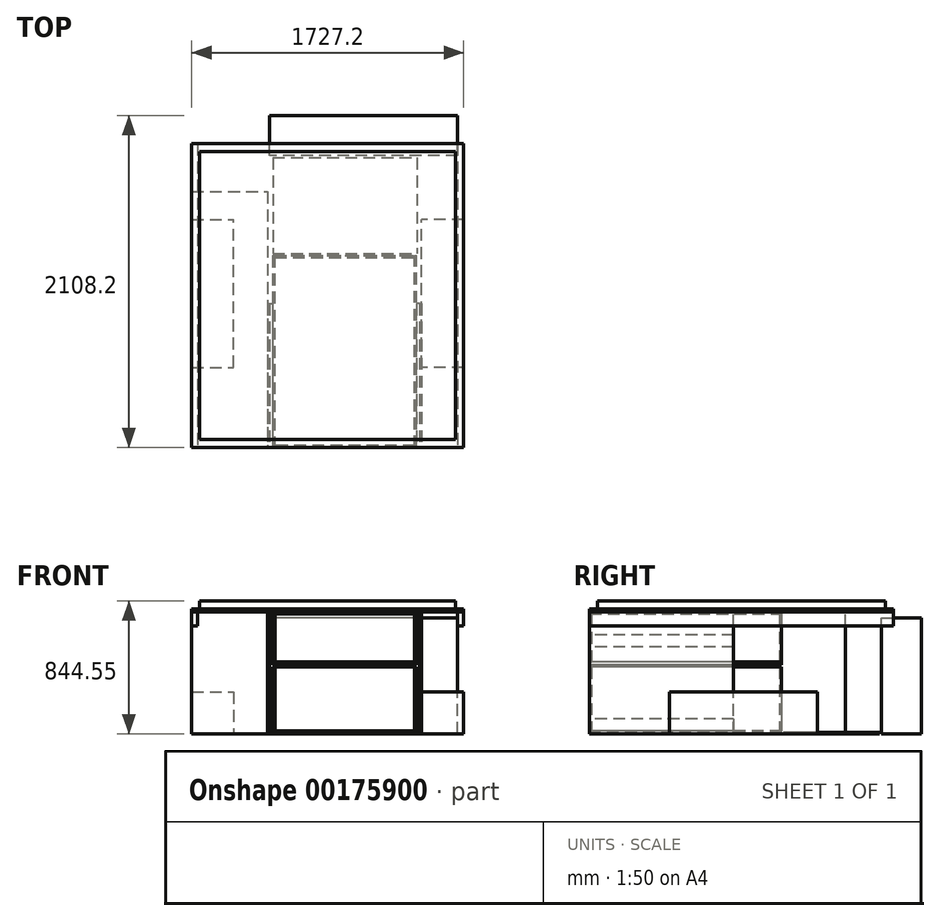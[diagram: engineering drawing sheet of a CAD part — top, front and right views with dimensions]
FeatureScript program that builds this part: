
annotation { "Feature Type Name" : "Feature", "Feature Type Description" : "" }
export const myFeature = defineFeature(function(context is Context, id is Id, definition is map)
    precondition{}
    {
        {
            var Q0;
            Q0=qCreatedBy(makeId("Front.planeOp"),FACE);
            var sketch = newSketch(context, id + "F0", { "sketchPlane" : qUnion([Q0])});
            skLineSegment(sketch, "E0.bottom", {"start": v(-863.6, 793.75) * mm, "end": v(863.6, 793.75) * mm});
            skLineSegment(sketch, "E0.top", {"start": v(-863.6, 774.7) * mm, "end": v(863.6, 774.7) * mm});
            skLineSegment(sketch, "E0.left", {"start": v(-863.6, 793.75) * mm, "end": v(-863.6, 774.7) * mm});
            skLineSegment(sketch, "E0.right", {"start": v(863.6, 793.75) * mm, "end": v(863.6, 774.7) * mm});
            skLineSegment(sketch, "E1", {"start": v(0, 774.7) * mm, "end": v(0, 0) * mm, "construction": true});
            skLineSegment(sketch, "E2.bottom", {"start": v(825.5, 774.45) * mm, "end": v(863.6, 774.45) * mm});
            skLineSegment(sketch, "E2.top", {"start": v(825.5, 685.55) * mm, "end": v(863.6, 685.55) * mm});
            skLineSegment(sketch, "E2.left", {"start": v(825.5, 774.45) * mm, "end": v(825.5, 685.55) * mm});
            skLineSegment(sketch, "E2.right", {"start": v(863.6, 774.45) * mm, "end": v(863.6, 685.55) * mm});
            skLineSegment(sketch, "E3.MirrorCS", {"start": v(-863.6, 774.45) * mm, "end": v(-863.6, 685.55) * mm});
            skLineSegment(sketch, "E4.MirrorCS", {"start": v(-825.5, 774.45) * mm, "end": v(-825.5, 685.55) * mm});
            skLineSegment(sketch, "E5.MirrorCS", {"start": v(-825.5, 774.45) * mm, "end": v(-863.6, 774.45) * mm});
            skLineSegment(sketch, "E6.MirrorCS", {"start": v(-825.5, 685.55) * mm, "end": v(-863.6, 685.55) * mm});
            skSolve(sketch);
        }
        {
            var Q0;
            Q0 = qSketchRegion(id + "F0", true);
            extrude(context, id + "F1", {"entities" : qUnion([Q0]), "oppositeDirection" : true, "depth" : 1930.4 * mm});
        }
        {
            var Q0;
            Q0=qCreatedBy(makeId("Top.planeOp"),FACE);
            var sketch = newSketch(context, id + "F2", { "sketchPlane" : qUnion([Q0])});
            skLineSegment(sketch, "E7.0.0", {"start": v(-863.6, 0) * mm, "end": v(863.6, 0) * mm});
            skLineSegment(sketch, "E7.0.1", {"start": v(863.6, 0) * mm, "end": v(863.6, 1930.4) * mm});
            skLineSegment(sketch, "E7.0.2", {"start": v(863.6, 1930.4) * mm, "end": v(-863.6, 1930.4) * mm});
            skLineSegment(sketch, "E7.0.3", {"start": v(-863.6, 1930.4) * mm, "end": v(-863.6, 0) * mm});
            skSolve(sketch);
        }
        {
            var Q0;
            Q0=qCreatedBy(makeId("Top.planeOp"),FACE);
            var sketch = newSketch(context, id + "F3", { "sketchPlane" : qUnion([Q0])});
            skLineSegment(sketch, "E8.bottom", {"start": v(863.6, 508) * mm, "end": v(596.9, 508) * mm});
            skLineSegment(sketch, "E8.top", {"start": v(863.6, 1447.8) * mm, "end": v(596.9, 1447.8) * mm});
            skLineSegment(sketch, "E8.left", {"start": v(863.6, 508) * mm, "end": v(863.6, 1447.8) * mm});
            skLineSegment(sketch, "E8.right", {"start": v(596.9, 508) * mm, "end": v(596.9, 1447.8) * mm});
            skLineSegment(sketch, "E9", {"start": v(0, 0) * mm, "end": v(0, 438.64) * mm, "construction": true});
            skLineSegment(sketch, "E10.MirrorCS", {"start": v(-863.6, 1447.8) * mm, "end": v(-596.9, 1447.8) * mm});
            skLineSegment(sketch, "E11.MirrorCS", {"start": v(-863.6, 508) * mm, "end": v(-596.9, 508) * mm});
            skLineSegment(sketch, "E12.MirrorCS", {"start": v(-863.6, 508) * mm, "end": v(-863.6, 1447.8) * mm});
            skLineSegment(sketch, "E13.MirrorCS", {"start": v(-596.9, 508) * mm, "end": v(-596.9, 1447.8) * mm});
            skSolve(sketch);
        }
        {
            var Q0;
            Q0 = qSketchRegion(id + "F3", true);
            extrude(context, id + "F4", {"entities" : qUnion([Q0]), "depth" : 266.7 * mm});
        }
        {
            var Q0;
            Q0=qCreatedBy(makeId("Front.planeOp"),FACE);
            var sketch = newSketch(context, id + "F5", { "sketchPlane" : qUnion([Q0])});
            skLineSegment(sketch, "E14.bottom", {"start": v(-381, 774.7) * mm, "end": v(-368.3, 774.7) * mm});
            skLineSegment(sketch, "E14.top", {"start": v(-381, 0) * mm, "end": v(-368.3, 0) * mm});
            skLineSegment(sketch, "E14.left", {"start": v(-381, 774.7) * mm, "end": v(-381, 0) * mm});
            skLineSegment(sketch, "E14.right", {"start": v(-368.3, 774.7) * mm, "end": v(-368.3, 0) * mm});
            skLineSegment(sketch, "E15.bottom", {"start": v(584.2, 0) * mm, "end": v(596.9, 0) * mm});
            skLineSegment(sketch, "E15.top", {"start": v(584.2, 774.7) * mm, "end": v(596.9, 774.7) * mm});
            skLineSegment(sketch, "E15.left", {"start": v(584.2, 0) * mm, "end": v(584.2, 774.7) * mm});
            skLineSegment(sketch, "E15.right", {"start": v(596.9, 0) * mm, "end": v(596.9, 774.7) * mm});
            skSolve(sketch);
        }
        {
            var Q0;
            Q0 = qSketchRegion(id + "F5", true);
            extrude(context, id + "F6", {"entities" : qUnion([Q0]), "oppositeDirection" : true, "depth" : 914.4 * mm});
        }
        {
            var Q0;
            Q0=qCreatedBy(makeId("Front.planeOp"),FACE);
            var sketch = newSketch(context, id + "F7", { "sketchPlane" : qUnion([Q0])});
            skLineSegment(sketch, "E16.bottom", {"start": v(-349.25, 95.25) * mm, "end": v(-368.3, 95.25) * mm});
            skLineSegment(sketch, "E16.top", {"start": v(-349.25, 19.05) * mm, "end": v(-368.3, 19.05) * mm});
            skLineSegment(sketch, "E16.left", {"start": v(-349.25, 95.25) * mm, "end": v(-349.25, 19.05) * mm});
            skLineSegment(sketch, "E16.right", {"start": v(-368.3, 95.25) * mm, "end": v(-368.3, 19.05) * mm});
            skLineSegment(sketch, "E17.bottom", {"start": v(565.15, 19.05) * mm, "end": v(584.2, 19.05) * mm});
            skLineSegment(sketch, "E17.top", {"start": v(565.15, 95.25) * mm, "end": v(584.2, 95.25) * mm});
            skLineSegment(sketch, "E17.left", {"start": v(565.15, 19.05) * mm, "end": v(565.15, 95.25) * mm});
            skLineSegment(sketch, "E17.right", {"start": v(584.2, 19.05) * mm, "end": v(584.2, 95.25) * mm});
            skLineSegment(sketch, "E18.bottom", {"start": v(-368.3, 628.65) * mm, "end": v(-349.25, 628.65) * mm});
            skLineSegment(sketch, "E18.top", {"start": v(-368.3, 552.45) * mm, "end": v(-349.25, 552.45) * mm});
            skLineSegment(sketch, "E18.left", {"start": v(-368.3, 628.65) * mm, "end": v(-368.3, 552.45) * mm});
            skLineSegment(sketch, "E18.right", {"start": v(-349.25, 628.65) * mm, "end": v(-349.25, 552.45) * mm});
            skPoint(sketch, "E18.middle", {"position": v(-358.78, 590.55) * mm});
            skLineSegment(sketch, "E19.bottom", {"start": v(584.2, 628.65) * mm, "end": v(565.15, 628.65) * mm});
            skLineSegment(sketch, "E19.top", {"start": v(584.2, 552.45) * mm, "end": v(565.15, 552.45) * mm});
            skLineSegment(sketch, "E19.left", {"start": v(584.2, 628.65) * mm, "end": v(584.2, 552.45) * mm});
            skLineSegment(sketch, "E19.right", {"start": v(565.15, 628.65) * mm, "end": v(565.15, 552.45) * mm});
            skPoint(sketch, "E19.middle", {"position": v(574.67, 590.55) * mm});
            skSolve(sketch);
        }
        {
            var Q0;
            Q0 = qSketchRegion(id + "F7", true);
            extrude(context, id + "F8", {"entities" : qUnion([Q0]), "oppositeDirection" : true, "depth" : 914.4 * mm});
        }
        {
            var Q0;
            Q0=qCreatedBy(makeId("Front.planeOp"),FACE);
            var sketch = newSketch(context, id + "F9", { "sketchPlane" : qUnion([Q0])});
            skLineSegment(sketch, "E20.bottom", {"start": v(-349.25, 9.52) * mm, "end": v(565.15, 9.53) * mm});
            skLineSegment(sketch, "E20.top", {"start": v(-349.25, 19.05) * mm, "end": v(565.15, 19.05) * mm});
            skLineSegment(sketch, "E20.left", {"start": v(-349.25, 9.53) * mm, "end": v(-349.25, 19.05) * mm});
            skLineSegment(sketch, "E20.right", {"start": v(565.15, 9.53) * mm, "end": v(565.15, 19.05) * mm});
            skSolve(sketch);
        }
        {
            var Q0;
            Q0=makeQuery(id+"F9.imprint","IMPRINT",FACE,{"disambiguationData":[TD([[makeQuery(id+"F9.imprint","IMPRINT",EDGE,{"derivedFrom":sQuery(id+"F9.wireOp",EDGE,"E20.bottom")}),1.0]])]});
            extrude(context, id + "F10", {"entities" : qUnion([Q0]), "oppositeDirection" : true, "depth" : 1219.2 * mm});
        }
        {
            var Q0;
            Q0=makeQuery(id+"F10.opExtrude","SWEPT_FACE",FACE,{"disambiguationData":[OSD([sQuery(id+"F9.wireOp",EDGE,"E20.top")])]});
            var sketch = newSketch(context, id + "F11", { "sketchPlane" : qUnion([Q0])});
            skLineSegment(sketch, "E21.bottom", {"start": v(-349.25, 1219.2) * mm, "end": v(-336.55, 1219.2) * mm});
            skLineSegment(sketch, "E21.top", {"start": v(-349.25, 0) * mm, "end": v(-336.55, 0) * mm});
            skLineSegment(sketch, "E21.left", {"start": v(-349.25, 1219.2) * mm, "end": v(-349.25, 0) * mm});
            skLineSegment(sketch, "E21.right", {"start": v(-336.55, 1219.2) * mm, "end": v(-336.55, 0) * mm});
            skLineSegment(sketch, "E22.bottom", {"start": v(565.15, 0) * mm, "end": v(552.45, 0) * mm});
            skLineSegment(sketch, "E22.top", {"start": v(565.15, 1219.2) * mm, "end": v(552.45, 1219.2) * mm});
            skLineSegment(sketch, "E22.left", {"start": v(565.15, 0) * mm, "end": v(565.15, 1219.2) * mm});
            skLineSegment(sketch, "E22.right", {"start": v(552.45, 0) * mm, "end": v(552.45, 1219.2) * mm});
            skLineSegment(sketch, "E23.bottom", {"start": v(-336.3, 1219.2) * mm, "end": v(552.2, 1219.2) * mm});
            skLineSegment(sketch, "E23.top", {"start": v(-336.3, 1206.5) * mm, "end": v(552.2, 1206.5) * mm});
            skLineSegment(sketch, "E23.left", {"start": v(552.2, 1219.2) * mm, "end": v(552.2, 1206.5) * mm});
            skLineSegment(sketch, "E23.right", {"start": v(-336.3, 1219.2) * mm, "end": v(-336.3, 1206.5) * mm});
            skLineSegment(sketch, "E24.bottom", {"start": v(552.2, 0) * mm, "end": v(-336.3, 0) * mm});
            skLineSegment(sketch, "E24.top", {"start": v(552.2, 12.7) * mm, "end": v(-336.3, 12.7) * mm});
            skLineSegment(sketch, "E24.left", {"start": v(552.2, 0) * mm, "end": v(552.2, 12.7) * mm});
            skLineSegment(sketch, "E24.right", {"start": v(-336.3, 0) * mm, "end": v(-336.3, 12.7) * mm});
            skSolve(sketch);
        }
        {
            var Q0;
            Q0 = qSketchRegion(id + "F11", true);
            extrude(context, id + "F12", {"entities" : qUnion([Q0]), "depth" : 406.4 * mm, "offsetDistance" : 25.4 * mm});
        }
        {
            var Q0;
            Q0=makeQuery(id+"F1.opExtrude","SWEPT_FACE",FACE,{"disambiguationData":[OSD([sQuery(id+"F0.wireOp",EDGE,"E0.bottom")])]});
            var sketch = newSketch(context, id + "F13", { "sketchPlane" : qUnion([Q0])});
            skLineSegment(sketch, "E25.0", {"start": v(-812.8, 50.8) * mm, "end": v(812.8, 50.8) * mm});
            skLineSegment(sketch, "E25.1", {"start": v(-812.8, 1879.6) * mm, "end": v(-812.8, 50.8) * mm});
            skLineSegment(sketch, "E25.2", {"start": v(812.8, 1879.6) * mm, "end": v(-812.8, 1879.6) * mm});
            skLineSegment(sketch, "E25.3", {"start": v(812.8, 50.8) * mm, "end": v(812.8, 1879.6) * mm});
            skSolve(sketch);
        }
        {
            var Q0;
            Q0 = qSketchRegion(id + "F13", true);
            extrude(context, id + "F14", {"entities" : qUnion([Q0]), "operationType" : NewBodyOperationType.ADD, "depth" : 50.8 * mm});
        }
        {
            var Q0;
            Q0=makeQuery(id+"F1.opExtrude","CAP_FACE",FACE,{"disambiguationData":[OSD([sQuery(id+"F0.wireOp",EDGE,"E0.bottom"),sQuery(id+"F0.wireOp",EDGE,"E0.top"),sQuery(id+"F0.wireOp",EDGE,"E0.left"),sQuery(id+"F0.wireOp",EDGE,"E0.right")])],"isStart":false});
            var sketch = newSketch(context, id + "F15", { "sketchPlane" : qUnion([Q0])});
            skLineSegment(sketch, "E26.bottom", {"start": v(-825.5, 0) * mm, "end": v(368.3, 0) * mm});
            skLineSegment(sketch, "E26.top", {"start": v(-825.5, 736.6) * mm, "end": v(368.3, 736.6) * mm});
            skLineSegment(sketch, "E26.left", {"start": v(-825.5, 0) * mm, "end": v(-825.5, 736.6) * mm});
            skLineSegment(sketch, "E26.right", {"start": v(368.3, 0) * mm, "end": v(368.3, 736.6) * mm});
            skSolve(sketch);
        }
        {
            var Q0;
            Q0 = qSketchRegion(id + "F15", true);
            extrude(context, id + "F16", {"entities" : qUnion([Q0]), "oppositeDirection" : true, "depth" : 76.2 * mm, "hasSecondDirection" : true, "secondDirectionOppositeDirection" : false, "secondDirectionDepth" : 177.8 * mm});
        }
        {
            var Q0;
            Q0=makeQuery(id+"F1.opExtrude","CAP_FACE",FACE,{"disambiguationData":[OSD([sQuery(id+"F0.wireOp",EDGE,"E3.MirrorCS"),sQuery(id+"F0.wireOp",EDGE,"E4.MirrorCS"),sQuery(id+"F0.wireOp",EDGE,"E5.MirrorCS"),sQuery(id+"F0.wireOp",EDGE,"E6.MirrorCS")])],"isStart":true});
            var sketch = newSketch(context, id + "F17", { "sketchPlane" : qUnion([Q0])});
            skLineSegment(sketch, "E27.bottom", {"start": v(-863.6, 0) * mm, "end": v(-381, 0) * mm});
            skLineSegment(sketch, "E27.top", {"start": v(-863.6, 774.7) * mm, "end": v(-381, 774.7) * mm});
            skLineSegment(sketch, "E27.left", {"start": v(-863.6, 0) * mm, "end": v(-863.6, 774.7) * mm});
            skLineSegment(sketch, "E27.right", {"start": v(-381, 0) * mm, "end": v(-381, 774.7) * mm});
            skSolve(sketch);
        }
        {
            var Q0;
            Q0 = qSketchRegion(id + "F17", true);
            extrude(context, id + "F18", {"entities" : qUnion([Q0]), "oppositeDirection" : true, "depth" : 1625.6 * mm});
        }
        {
            var Q0;
            Q0=qCreatedBy(makeId("Top.planeOp"),FACE);
            var sketch = newSketch(context, id + "F19", { "sketchPlane" : qUnion([Q0])});
            skLineSegment(sketch, "E28.bottom", {"start": v(-348.45, 1841.16) * mm, "end": v(565.95, 1841.16) * mm});
            skLineSegment(sketch, "E28.top", {"start": v(-348.45, 1231.56) * mm, "end": v(565.95, 1231.56) * mm});
            skLineSegment(sketch, "E28.left", {"start": v(-348.45, 1841.16) * mm, "end": v(-348.45, 1231.56) * mm});
            skLineSegment(sketch, "E28.right", {"start": v(565.95, 1841.16) * mm, "end": v(565.95, 1231.56) * mm});
            skSolve(sketch);
        }
        {
            var Q0;
            Q0 = qSketchRegion(id + "F19", true);
            extrude(context, id + "F20", {"entities" : qUnion([Q0]), "depth" : 9.52 * mm});
        }
        {
            var Q0;
            Q0=makeQuery(id+"F10.opExtrude","CAP_FACE",FACE,{"disambiguationData":[OSD([sQuery(id+"F9.wireOp",EDGE,"E20.bottom"),sQuery(id+"F9.wireOp",EDGE,"E20.top"),sQuery(id+"F9.wireOp",EDGE,"E20.left"),sQuery(id+"F9.wireOp",EDGE,"E20.right")])],"isStart":true});
            var sketch = newSketch(context, id + "F21", { "sketchPlane" : qUnion([Q0])});
            skLineSegment(sketch, "E29.bottom", {"start": v(-349.25, 438.15) * mm, "end": v(565.15, 438.15) * mm});
            skLineSegment(sketch, "E29.top", {"start": v(-349.25, 457.2) * mm, "end": v(565.15, 457.2) * mm});
            skLineSegment(sketch, "E29.left", {"start": v(-349.25, 438.15) * mm, "end": v(-349.25, 457.2) * mm});
            skLineSegment(sketch, "E29.right", {"start": v(565.15, 438.15) * mm, "end": v(565.15, 457.2) * mm});
            skSolve(sketch);
        }
        {
            var Q0;
            Q0=makeQuery(id+"F21.imprint","IMPRINT",FACE,{"disambiguationData":[TD([[makeQuery(id+"F21.imprint","IMPRINT",EDGE,{"derivedFrom":sQuery(id+"F21.wireOp",EDGE,"E29.bottom")}),1.0]])]});
            var Q1;
            Q1=makeQuery(id+"F10.opExtrude","CAP_FACE",FACE,{"disambiguationData":[OSD([sQuery(id+"F9.wireOp",EDGE,"E20.bottom"),sQuery(id+"F9.wireOp",EDGE,"E20.top"),sQuery(id+"F9.wireOp",EDGE,"E20.left"),sQuery(id+"F9.wireOp",EDGE,"E20.right")])],"isStart":false});
            extrude(context, id + "F22", {"entities" : qUnion([Q0]), "endBound" : BoundingType.UP_TO_SURFACE, "oppositeDirection" : true, "depth" : 25.4 * mm, "endBoundEntityFace" : qUnion([Q1]), "offsetDistance" : 25.4 * mm});
        }
        {
            var Q0;
            Q0=makeQuery(id+"F22.opExtrude","SWEPT_FACE",FACE,{"disambiguationData":[OSD([sQuery(id+"F21.wireOp",EDGE,"E29.top")])]});
            var sketch = newSketch(context, id + "F23", { "sketchPlane" : qUnion([Q0])});
            skLineSegment(sketch, "E30.bottom", {"start": v(-349.25, 0) * mm, "end": v(-336.55, 0) * mm});
            skLineSegment(sketch, "E30.top", {"start": v(-349.25, 1219.2) * mm, "end": v(-336.55, 1219.2) * mm});
            skLineSegment(sketch, "E30.left", {"start": v(-349.25, 0) * mm, "end": v(-349.25, 1219.2) * mm});
            skLineSegment(sketch, "E30.right", {"start": v(-336.55, 0) * mm, "end": v(-336.55, 1219.2) * mm});
            skLineSegment(sketch, "E31.bottom", {"start": v(565.15, 1219.2) * mm, "end": v(552.45, 1219.2) * mm});
            skLineSegment(sketch, "E31.top", {"start": v(565.15, 0) * mm, "end": v(552.45, 0) * mm});
            skLineSegment(sketch, "E31.left", {"start": v(565.15, 1219.2) * mm, "end": v(565.15, 0) * mm});
            skLineSegment(sketch, "E31.right", {"start": v(552.45, 1219.2) * mm, "end": v(552.45, 0) * mm});
            skLineSegment(sketch, "E32.bottom", {"start": v(-336.3, 0) * mm, "end": v(552.2, 0) * mm});
            skLineSegment(sketch, "E32.top", {"start": v(-336.3, 12.7) * mm, "end": v(552.2, 12.7) * mm});
            skLineSegment(sketch, "E32.left", {"start": v(-336.3, 0) * mm, "end": v(-336.3, 12.7) * mm});
            skLineSegment(sketch, "E32.right", {"start": v(552.2, 0) * mm, "end": v(552.2, 12.7) * mm});
            skLineSegment(sketch, "E33.bottom", {"start": v(552.2, 1219.2) * mm, "end": v(-336.3, 1219.2) * mm});
            skLineSegment(sketch, "E33.top", {"start": v(552.2, 1206.5) * mm, "end": v(-336.3, 1206.5) * mm});
            skLineSegment(sketch, "E33.left", {"start": v(552.2, 1219.2) * mm, "end": v(552.2, 1206.5) * mm});
            skLineSegment(sketch, "E33.right", {"start": v(-336.3, 1219.2) * mm, "end": v(-336.3, 1206.5) * mm});
            skSolve(sketch);
        }
        {
            var Q0;
            Q0 = qSketchRegion(id + "F23", true);
            var Q1;
            Q1=makeQuery(id+"F1.opExtrude","SWEPT_FACE",FACE,{"disambiguationData":[OSD([sQuery(id+"F0.wireOp",EDGE,"E0.top")])]});
            extrude(context, id + "F24", {"entities" : qUnion([Q0]), "endBound" : BoundingType.UP_TO_SURFACE, "depth" : 25.4 * mm, "endBoundEntityFace" : qUnion([Q1]), "hasOffset" : true, "offsetDistance" : 12.7 * mm});
        }
    });
